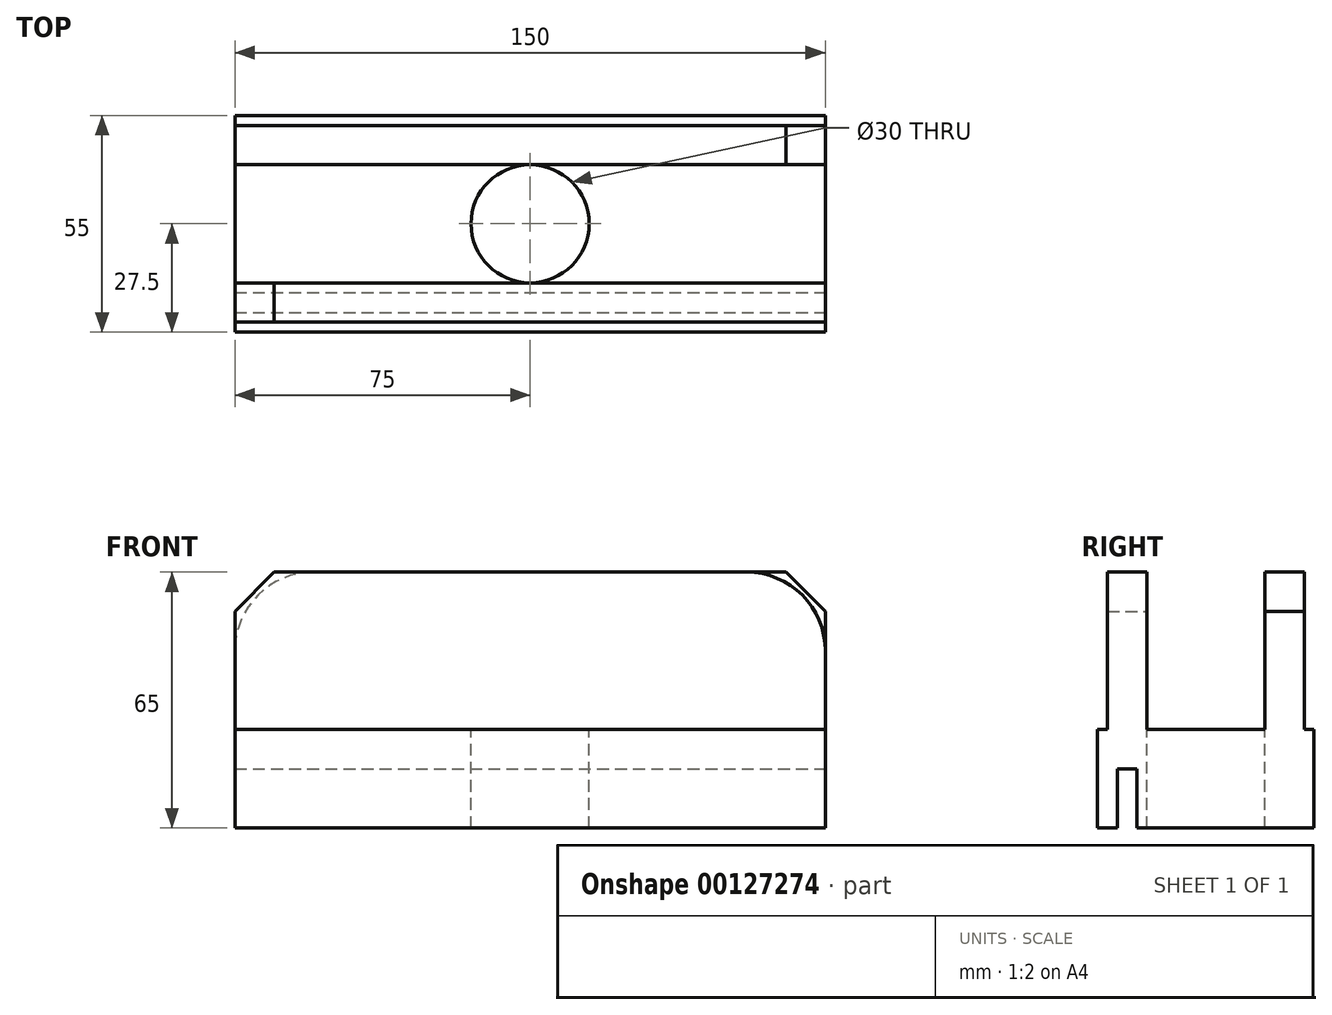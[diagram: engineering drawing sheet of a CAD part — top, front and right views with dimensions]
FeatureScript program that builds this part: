
annotation { "Feature Type Name" : "Feature", "Feature Type Description" : "" }
export const myFeature = defineFeature(function(context is Context, id is Id, definition is map)
    precondition{}
    {
        {
            var Q0;
            Q0=qCreatedBy(makeId("Front.planeOp"),FACE);
            var sketch = newSketch(context, id + "F0", { "sketchPlane" : qUnion([Q0])});
            skLineSegment(sketch, "E0.bottom", {"start": v(75, 32.5) * mm, "end": v(-75, 32.5) * mm});
            skLineSegment(sketch, "E0.top", {"start": v(75, -32.5) * mm, "end": v(-75, -32.5) * mm});
            skLineSegment(sketch, "E0.left", {"start": v(75, 32.5) * mm, "end": v(75, -32.5) * mm});
            skLineSegment(sketch, "E0.right", {"start": v(-75, 32.5) * mm, "end": v(-75, -32.5) * mm});
            skPoint(sketch, "E0.middle", {"position": v(0, 0) * mm});
            skSolve(sketch);
        }
        {
            var Q0;
            Q0 = qSketchRegion(id + "F0", true);
            extrude(context, id + "F1", {"entities" : qUnion([Q0]), "depth" : 55 * mm});
        }
        {
            var Q0;
            Q0=makeQuery(id+"F1.opExtrude","SWEPT_FACE",FACE,{"disambiguationData":[OSD([sQuery(id+"F0.wireOp",EDGE,"E0.left")])]});
            var sketch = newSketch(context, id + "F2", { "sketchPlane" : qUnion([Q0])});
            skLineSegment(sketch, "E1.bottom", {"start": v(-50, -32.5) * mm, "end": v(-45, -32.5) * mm});
            skLineSegment(sketch, "E1.top", {"start": v(-50, -17.5) * mm, "end": v(-45, -17.5) * mm});
            skLineSegment(sketch, "E1.left", {"start": v(-50, -32.5) * mm, "end": v(-50, -17.5) * mm});
            skLineSegment(sketch, "E1.right", {"start": v(-45, -32.5) * mm, "end": v(-45, -17.5) * mm});
            skSolve(sketch);
        }
        {
            var Q0;
            Q0 = qSketchRegion(id + "F2", true);
            extrude(context, id + "F3", {"entities" : qUnion([Q0]), "operationType" : NewBodyOperationType.REMOVE, "endBound" : BoundingType.THROUGH_ALL, "oppositeDirection" : true, "depth" : 25.4 * mm});
        }
        {
            var Q0;
            Q0=makeQuery(id+"F1.opExtrude","SWEPT_FACE",FACE,{"disambiguationData":[OSD([sQuery(id+"F0.wireOp",EDGE,"E0.left")])]});
            var sketch = newSketch(context, id + "F4", { "sketchPlane" : qUnion([Q0])});
            skLineSegment(sketch, "E2.bottom", {"start": v(-42.5, 32.5) * mm, "end": v(-12.5, 32.5) * mm});
            skLineSegment(sketch, "E2.top", {"start": v(-42.5, -7.5) * mm, "end": v(-12.5, -7.5) * mm});
            skLineSegment(sketch, "E2.left", {"start": v(-42.5, 32.5) * mm, "end": v(-42.5, -7.5) * mm});
            skLineSegment(sketch, "E2.right", {"start": v(-12.5, 32.5) * mm, "end": v(-12.5, -7.5) * mm});
            skSolve(sketch);
        }
        {
            var Q0;
            Q0 = qSketchRegion(id + "F4", true);
            extrude(context, id + "F5", {"entities" : qUnion([Q0]), "operationType" : NewBodyOperationType.REMOVE, "endBound" : BoundingType.THROUGH_ALL, "oppositeDirection" : true, "depth" : 25.4 * mm});
        }
        {
            var Q0;
            {var subQ0=sQuery(id+"F0.wireOp",EDGE,"E0.bottom");var subQ1=sQuery(id+"F0.wireOp",EDGE,"E0.left");Q0=makeQuery(id+"F5.boolean.opBoolean","SPLIT",EDGE,{"disambiguationData":[TD([makeQuery(id+"F5.opExtrude","SWEPT_FACE",FACE,{"disambiguationData":[OSD([sQuery(id+"F4.wireOp",EDGE,"E2.right")])]})])],"derivedFrom":makeQuery(id+"F1.opExtrude","SWEPT_EDGE",EDGE,{"disambiguationData":[OSD([subQ0,subQ1])]})});}
            var Q1;
            {var subQ0=sQuery(id+"F0.wireOp",EDGE,"E0.bottom");var subQ1=sQuery(id+"F0.wireOp",EDGE,"E0.right");Q1=makeQuery(id+"F5.boolean.opBoolean","SPLIT",EDGE,{"disambiguationData":[TD([makeQuery(id+"F5.opExtrude","SWEPT_FACE",FACE,{"disambiguationData":[OSD([sQuery(id+"F4.wireOp",EDGE,"E2.left")])]})])],"derivedFrom":makeQuery(id+"F1.opExtrude","SWEPT_EDGE",EDGE,{"disambiguationData":[OSD([subQ0,subQ1])]})});}
            chamfer(context, id + "F6", {"entities" : qUnion([Q0, Q1]), "width" : 10 * mm, "tangentPropagation" : true});
        }
        {
            var Q0;
            {var subQ0=sQuery(id+"F0.wireOp",EDGE,"E0.bottom");var subQ1=sQuery(id+"F0.wireOp",EDGE,"E0.left");Q0=makeQuery(id+"F5.boolean.opBoolean","SPLIT",EDGE,{"disambiguationData":[TD([makeQuery(id+"F5.opExtrude","SWEPT_FACE",FACE,{"disambiguationData":[OSD([sQuery(id+"F4.wireOp",EDGE,"E2.left")])]})])],"derivedFrom":makeQuery(id+"F1.opExtrude","SWEPT_EDGE",EDGE,{"disambiguationData":[OSD([subQ0,subQ1])]})});}
            var Q1;
            {var subQ0=sQuery(id+"F0.wireOp",EDGE,"E0.bottom");var subQ1=sQuery(id+"F0.wireOp",EDGE,"E0.right");Q1=makeQuery(id+"F5.boolean.opBoolean","SPLIT",EDGE,{"disambiguationData":[TD([makeQuery(id+"F5.opExtrude","SWEPT_FACE",FACE,{"disambiguationData":[OSD([sQuery(id+"F4.wireOp",EDGE,"E2.right")])]})])],"derivedFrom":makeQuery(id+"F1.opExtrude","SWEPT_EDGE",EDGE,{"disambiguationData":[OSD([subQ0,subQ1])]})});}
            fillet(context, id + "F7", {"entities" : qUnion([Q0, Q1]), "radius" : 20 * mm, "tangentPropagation" : true, "allowEdgeOverflow" : false});
        }
        {
            var Q0;
            Q0=makeQuery(id+"F1.opExtrude","SWEPT_FACE",FACE,{"disambiguationData":[OSD([sQuery(id+"F0.wireOp",EDGE,"E0.left")])]});
            var sketch = newSketch(context, id + "F8", { "sketchPlane" : qUnion([Q0])});
            skLineSegment(sketch, "E3.bottom", {"start": v(-55, -7.5) * mm, "end": v(-52.5, -7.5) * mm});
            skLineSegment(sketch, "E3.top", {"start": v(-55, 35.8) * mm, "end": v(-52.5, 35.8) * mm});
            skLineSegment(sketch, "E3.left", {"start": v(-55, -7.5) * mm, "end": v(-55, 35.8) * mm});
            skLineSegment(sketch, "E3.right", {"start": v(-52.5, -7.5) * mm, "end": v(-52.5, 35.8) * mm});
            skSolve(sketch);
        }
        {
            var Q0;
            Q0 = qSketchRegion(id + "F8", true);
            extrude(context, id + "F9", {"entities" : qUnion([Q0]), "operationType" : NewBodyOperationType.REMOVE, "endBound" : BoundingType.THROUGH_ALL, "oppositeDirection" : true, "depth" : 25.4 * mm});
        }
        {
            var Q0;
            Q0=makeQuery(id+"F1.opExtrude","SWEPT_FACE",FACE,{"disambiguationData":[OSD([sQuery(id+"F0.wireOp",EDGE,"E0.left")])]});
            var sketch = newSketch(context, id + "F10", { "sketchPlane" : qUnion([Q0])});
            skLineSegment(sketch, "E4.bottom", {"start": v(0, -7.5) * mm, "end": v(-2.5, -7.5) * mm});
            skLineSegment(sketch, "E4.top", {"start": v(0, 35.97) * mm, "end": v(-2.5, 35.97) * mm});
            skLineSegment(sketch, "E4.left", {"start": v(0, -7.5) * mm, "end": v(0, 35.97) * mm});
            skLineSegment(sketch, "E4.right", {"start": v(-2.5, -7.5) * mm, "end": v(-2.5, 35.97) * mm});
            skSolve(sketch);
        }
        {
            var Q0;
            Q0 = qSketchRegion(id + "F10", true);
            extrude(context, id + "F11", {"entities" : qUnion([Q0]), "operationType" : NewBodyOperationType.REMOVE, "endBound" : BoundingType.THROUGH_ALL, "oppositeDirection" : true, "depth" : 25.4 * mm});
        }
        {
            var Q0;
            Q0=makeQuery(id+"F5.boolean.opBoolean","COPY",FACE,{"derivedFrom":makeQuery(id+"F5.opExtrude","SWEPT_FACE",FACE,{"disambiguationData":[OSD([sQuery(id+"F4.wireOp",EDGE,"E2.top")])]})});
            var sketch = newSketch(context, id + "F12", { "sketchPlane" : qUnion([Q0])});
            skCircle(sketch, "E5", {"center": v(0, -27.5) * mm, "radius": 15 * mm});
            skSolve(sketch);
        }
        {
            var Q0;
            Q0 = qSketchRegion(id + "F12", true);
            extrude(context, id + "F13", {"entities" : qUnion([Q0]), "operationType" : NewBodyOperationType.REMOVE, "endBound" : BoundingType.THROUGH_ALL, "oppositeDirection" : true, "depth" : 25.4 * mm});
        }
    });
